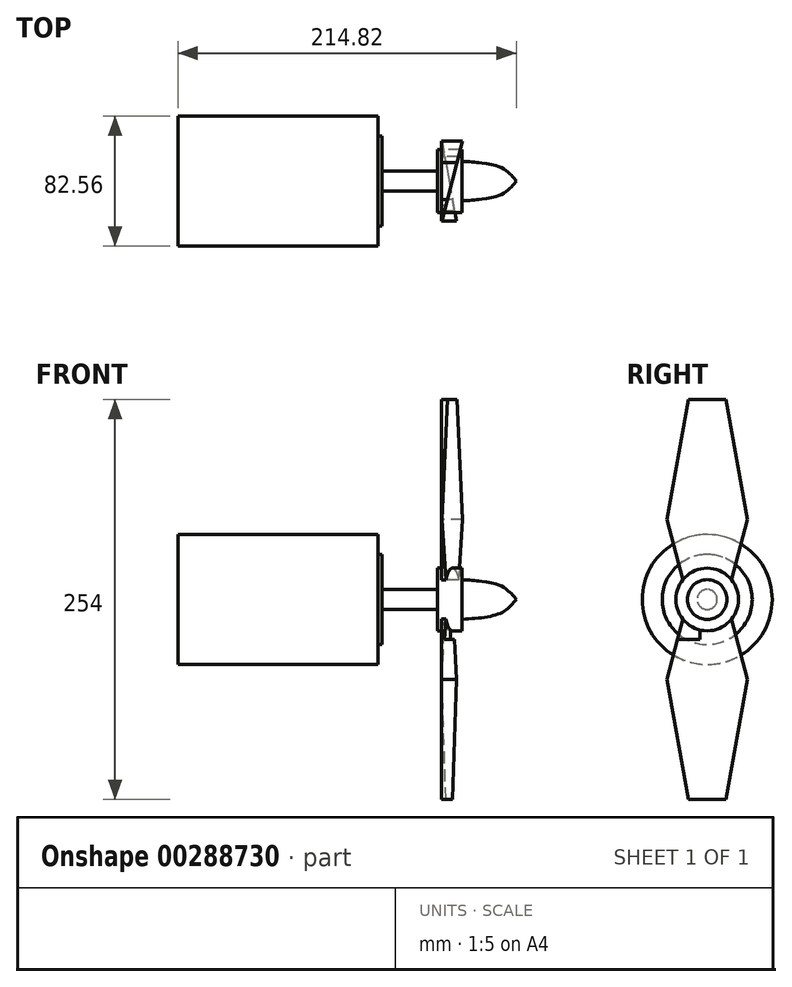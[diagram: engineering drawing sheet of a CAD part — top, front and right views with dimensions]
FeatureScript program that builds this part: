
annotation { "Feature Type Name" : "Feature", "Feature Type Description" : "" }
export const myFeature = defineFeature(function(context is Context, id is Id, definition is map)
    precondition{}
    {
        {
            var Q0;
            Q0=qCreatedBy(makeId("Right.planeOp"),FACE);
            var sketch = newSketch(context, id + "F0", { "sketchPlane" : qUnion([Q0])});
            skArc(sketch, "E0", {"start": v(-15.24, 11.43) * mm, "mid": v(-19.05, 0) * mm, "end": v(-15.24, -11.43) * mm});
            skLineSegment(sketch, "E1", {"start": v(15.24, 11.43) * mm, "end": v(25.4, 50.8) * mm});
            skLineSegment(sketch, "E2", {"start": v(25.4, 50.8) * mm, "end": v(11.88, 127) * mm});
            skLineSegment(sketch, "E3", {"start": v(11.88, 127) * mm, "end": v(0, 127) * mm});
            skLineSegment(sketch, "E4.MirrorCS", {"start": v(-11.88, 127) * mm, "end": v(0, 127) * mm});
            skLineSegment(sketch, "E5.MirrorCS", {"start": v(-15.24, 11.43) * mm, "end": v(-25.4, 50.8) * mm});
            skLineSegment(sketch, "E6.MirrorCS", {"start": v(-25.4, 50.8) * mm, "end": v(-11.88, 127) * mm});
            skLineSegment(sketch, "E7.MirrorCS", {"start": v(-15.24, -11.43) * mm, "end": v(-25.4, -50.8) * mm});
            skLineSegment(sketch, "E8.MirrorCS", {"start": v(-25.4, -50.8) * mm, "end": v(-11.88, -127) * mm});
            skLineSegment(sketch, "E9.MirrorCS", {"start": v(-11.88, -127) * mm, "end": v(0, -127) * mm});
            skLineSegment(sketch, "E10.MirrorCS", {"start": v(11.88, -127) * mm, "end": v(0, -127) * mm});
            skLineSegment(sketch, "E11.MirrorCS", {"start": v(25.4, -50.8) * mm, "end": v(11.88, -127) * mm});
            skLineSegment(sketch, "E12.MirrorCS", {"start": v(15.24, -11.43) * mm, "end": v(25.4, -50.8) * mm});
            skArc(sketch, "E13.trimOffspring", {"start": v(15.24, -11.43) * mm, "mid": v(19.05, 0) * mm, "end": v(15.24, 11.43) * mm});
            skSolve(sketch);
        }
        {
            var Q0;
            Q0 = qSketchRegion(id + "F0", true);
            extrude(context, id + "F1", {"entities" : qUnion([Q0]), "endBound" : BoundingType.SYMMETRIC, "depth" : 25.4 * mm});
        }
        {
            var Q0;
            Q0=qCreatedBy(makeId("Top.planeOp"),FACE);
            var sketch = newSketch(context, id + "F2", { "sketchPlane" : qUnion([Q0])});
            skLineSegment(sketch, "E14", {"start": v(-14.06, 34.22) * mm, "end": v(15.04, -126.27) * mm});
            skLineSegment(sketch, "E15", {"start": v(15.04, -126.27) * mm, "end": v(15.04, 34.22) * mm});
            skLineSegment(sketch, "E16", {"start": v(15.04, 34.22) * mm, "end": v(-14.06, 34.22) * mm});
            skSolve(sketch);
        }
        {
            var Q0;
            Q0 = qSketchRegion(id + "F2", true);
            extrude(context, id + "F3", {"entities" : qUnion([Q0]), "operationType" : NewBodyOperationType.REMOVE, "oppositeDirection" : true, "depth" : 254 * mm});
        }
        {
            var Q0;
            Q0=qCreatedBy(makeId("Top.planeOp"),FACE);
            var sketch = newSketch(context, id + "F4", { "sketchPlane" : qUnion([Q0])});
            skLineSegment(sketch, "E17", {"start": v(-13.91, -30.98) * mm, "end": v(7.27, 50.54) * mm});
            skLineSegment(sketch, "E18", {"start": v(7.27, 50.54) * mm, "end": v(33.82, -30.98) * mm});
            skLineSegment(sketch, "E19", {"start": v(33.82, -30.98) * mm, "end": v(-13.91, -30.98) * mm});
            skSolve(sketch);
        }
        {
            var Q0;
            Q0 = qSketchRegion(id + "F4", true);
            extrude(context, id + "F5", {"entities" : qUnion([Q0]), "operationType" : NewBodyOperationType.REMOVE, "depth" : 254 * mm, "hasSecondDirection" : true, "secondDirectionOppositeDirection" : true, "secondDirectionDepth" : 25.4 * mm});
        }
        {
            var Q0;
            Q0=qCreatedBy(makeId("Right.planeOp"),FACE);
            var sketch = newSketch(context, id + "F6", { "sketchPlane" : qUnion([Q0])});
            skCircle(sketch, "E20", {"center": v(0, 0) * mm, "radius": 19.9 * mm});
            skSolve(sketch);
        }
        {
            var Q0;
            Q0 = qSketchRegion(id + "F6", true);
            extrude(context, id + "F7", {"entities" : qUnion([Q0]), "operationType" : NewBodyOperationType.ADD, "depth" : 0.25 * mm, "hasSecondDirection" : true, "secondDirectionOppositeDirection" : true, "secondDirectionDepth" : 15.24 * mm});
        }
        {
            var Q0;
            Q0=makeQuery(id+"F7.opExtrude","CAP_FACE",FACE,{"disambiguationData":[OSD([sQuery(id+"F6.wireOp",EDGE,"E20")])],"isStart":false});
            var sketch = newSketch(context, id + "F8", { "sketchPlane" : qUnion([Q0])});
            skCircle(sketch, "E21", {"center": v(0, 0) * mm, "radius": 6.35 * mm});
            skSolve(sketch);
        }
        {
            var Q0;
            Q0 = qSketchRegion(id + "F8", true);
            extrude(context, id + "F9", {"entities" : qUnion([Q0]), "operationType" : NewBodyOperationType.REMOVE, "oppositeDirection" : true, "depth" : 25.4 * mm});
        }
        {
            var Q0;
            Q0 = qSketchRegion(id + "F8", true);
            extrude(context, id + "F10", {"entities" : qUnion([Q0]), "operationType" : NewBodyOperationType.ADD, "depth" : 12.7 * mm, "hasSecondDirection" : true, "secondDirectionOppositeDirection" : true, "secondDirectionDepth" : 76.2 * mm});
        }
        {
            var Q0;
            Q0=makeQuery(id+"F10.opExtrude","CAP_FACE",FACE,{"disambiguationData":[OSD([sQuery(id+"F8.wireOp",EDGE,"E21")])],"isStart":true});
            var sketch = newSketch(context, id + "F11", { "sketchPlane" : qUnion([Q0])});
            skCircle(sketch, "E22", {"center": v(0, 0) * mm, "radius": 28.58 * mm});
            skSolve(sketch);
        }
        {
            var Q0;
            Q0 = qSketchRegion(id + "F11", true);
            extrude(context, id + "F12", {"entities" : qUnion([Q0]), "operationType" : NewBodyOperationType.ADD, "depth" : 2.54 * mm, "hasSecondDirection" : true, "secondDirectionOppositeDirection" : true, "secondDirectionDepth" : 25.4 * mm});
        }
        {
            var Q0;
            Q0=makeQuery(id+"F12.opExtrude","CAP_FACE",FACE,{"disambiguationData":[OSD([sQuery(id+"F11.wireOp",EDGE,"E22")])],"isStart":false});
            var sketch = newSketch(context, id + "F13", { "sketchPlane" : qUnion([Q0])});
            skCircle(sketch, "E23", {"center": v(0, 0) * mm, "radius": 41.28 * mm});
            skSolve(sketch);
        }
        {
            var Q0;
            Q0 = qSketchRegion(id + "F13", true);
            extrude(context, id + "F14", {"entities" : qUnion([Q0]), "operationType" : NewBodyOperationType.ADD, "depth" : 101.6 * mm, "hasSecondDirection" : true, "secondDirectionOppositeDirection" : true, "secondDirectionDepth" : 25.4 * mm});
        }
        {
            var Q0;
            Q0=qCreatedBy(makeId("Front.planeOp"),FACE);
            var sketch = newSketch(context, id + "F15", { "sketchPlane" : qUnion([Q0])});
            skLineSegment(sketch, "E24", {"start": v(0, 0) * mm, "end": v(34.73, 0) * mm});
            skFitSpline(sketch, "E25", {"points": [v(34.73, 0) * mm, v(25.21, -8.47) * mm, v(0, -12.6) * mm], "startDerivative": vector(-18.84, -23.25) * mm, "endDerivative": vector(-48.89, -3.13) * mm});
            skLineSegment(sketch, "E26", {"start": v(0, -12.6) * mm, "end": v(0, 0) * mm});
            skSolve(sketch);
        }
        {
            var Q0;
            Q0 = qSketchRegion(id + "F15", true);
            var Q1;
            Q1=sQuery(id+"F15.wireOp",EDGE,"E24");
            revolve(context, id + "F16", {"operationType" : NewBodyOperationType.ADD, "entities" : qUnion([Q0]), "axis" : qUnion([Q1]), "revolveType" : RevolveType.FULL});
        }
    });
